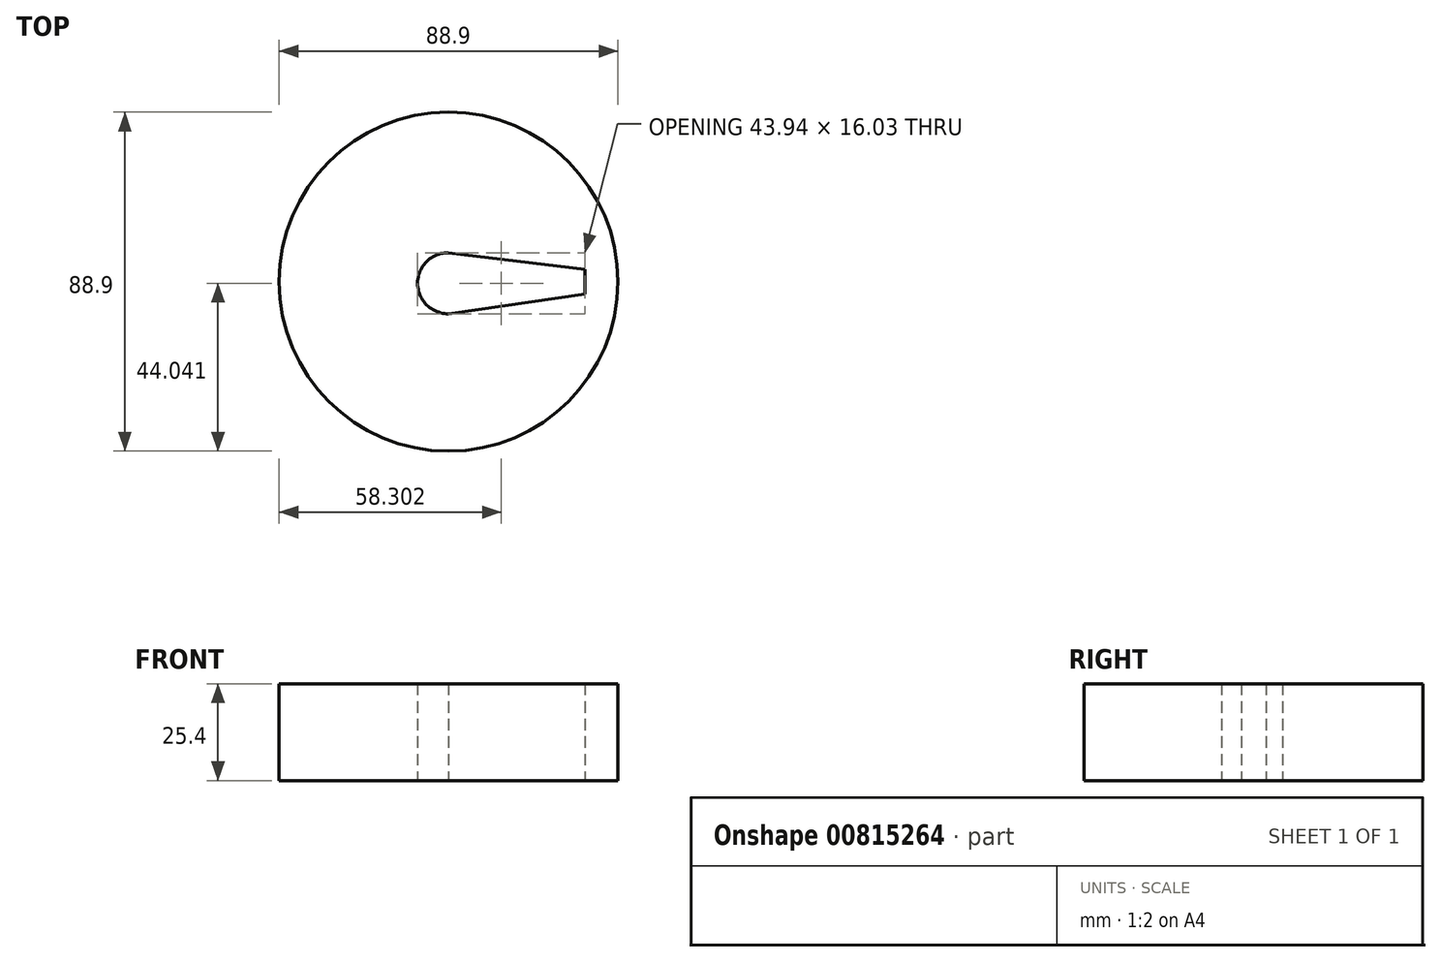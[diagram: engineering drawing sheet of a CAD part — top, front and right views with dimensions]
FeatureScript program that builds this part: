
annotation { "Feature Type Name" : "Feature", "Feature Type Description" : "" }
export const myFeature = defineFeature(function(context is Context, id is Id, definition is map)
    precondition{}
    {
        {
            var Q0;
            Q0=qCreatedBy(makeId("Top.planeOp"),FACE);
            var sketch = newSketch(context, id + "F0", { "sketchPlane" : qUnion([Q0])});
            skLineSegment(sketch, "E0", {"start": v(35.82, 3.24) * mm, "end": v(35.82, -3.24) * mm});
            skLineSegment(sketch, "E1", {"start": v(35.82, 3.24) * mm, "end": v(0, 7.6) * mm});
            skLineSegment(sketch, "E2", {"start": v(35.82, -3.24) * mm, "end": v(0, -8.42) * mm});
            skArc(sketch, "E3", {"start": v(0, 7.6) * mm, "mid": v(-8.12, -0.4) * mm, "end": v(0, -8.42) * mm});
            skCircle(sketch, "E4", {"center": v(0, 0) * mm, "radius": 44.45 * mm});
            skSolve(sketch);
        }
        {
            var Q0;
            Q0=makeQuery(id+"F0.imprint","IMPRINT",FACE,{"disambiguationData":[TD([[makeQuery(id+"F0.imprint","IMPRINT",EDGE,{"derivedFrom":sQuery(id+"F0.wireOp",EDGE,"E0")}),1.0]])]});
            extrude(context, id + "F1", {"entities" : qUnion([Q0]), "depth" : 25.4 * mm, "offsetDistance" : 25.4 * mm});
        }
    });
